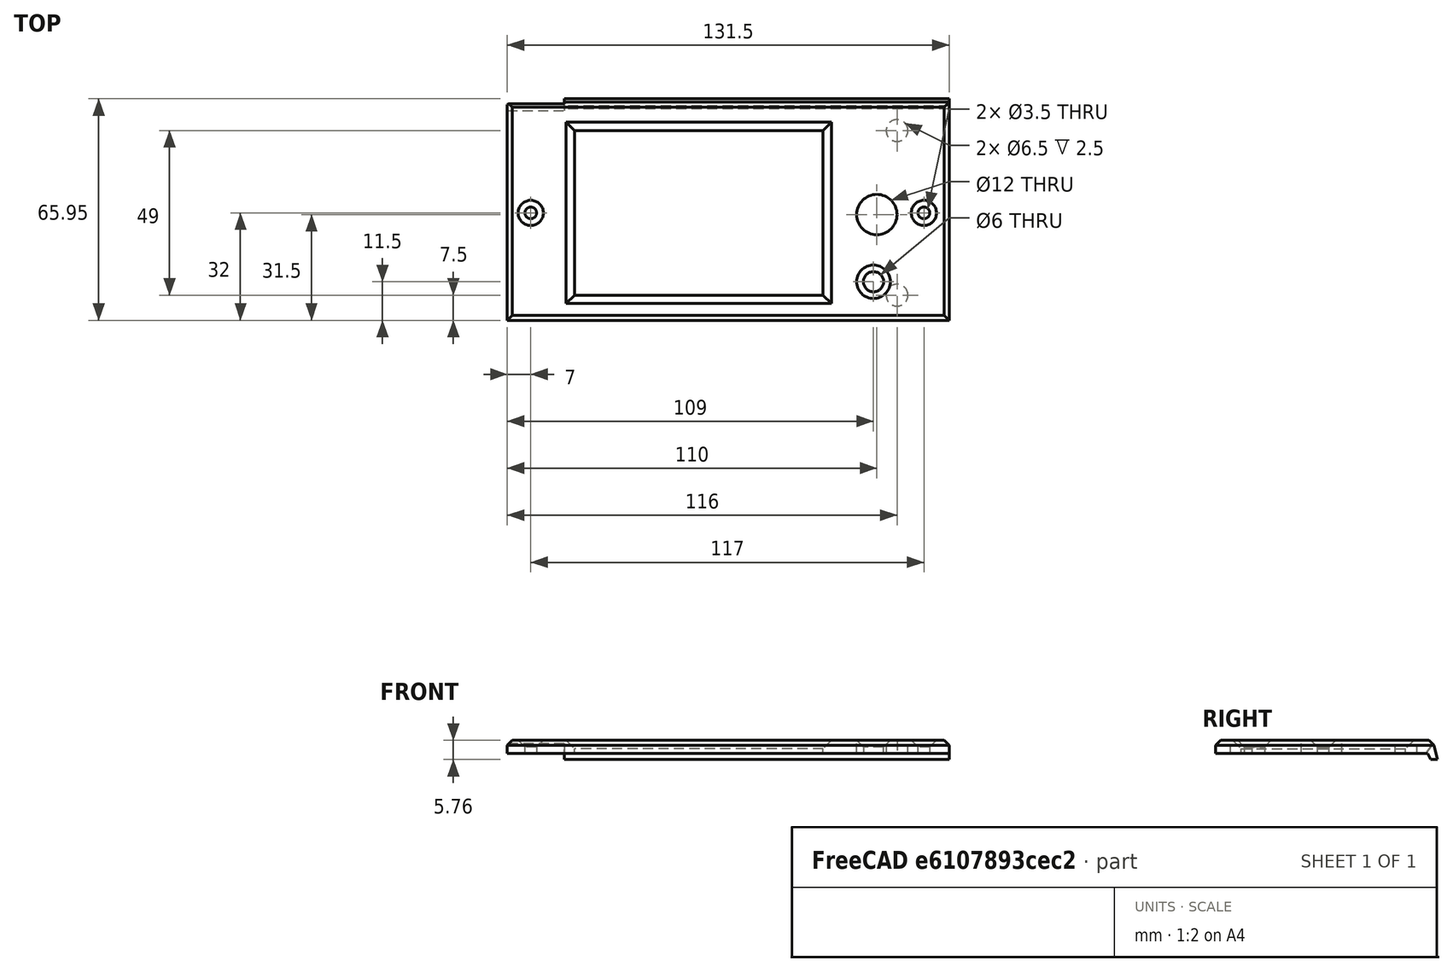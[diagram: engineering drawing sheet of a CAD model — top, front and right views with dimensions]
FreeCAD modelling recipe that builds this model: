
FCSTD DOCUMENT  (FreeCAD 0.19R)
Label: ScreenBezel
License: All rights reserved
LicenseURL: http://en.wikipedia.org/wiki/All_rights_reserved
objects: Sketcher::SketchObject×7, PartDesign::Pocket×5, PartDesign::Chamfer×4, PartDesign::Pad×2, PartDesign::Body×1, Mesh::Feature×1
note: 30 computed .brp shape members not serialized (recipe doc carries the construction recipe); baked Part::Feature solids carry a one-line shape summary decoded from their .brp

FEATURE [Sketcher::SketchObject] Sketch
  FullyConstrained = true
  MapMode = 5
  Support = -> [XY_Plane]
  sketch-geometry (8):
    g0: LineSegment StartX=-59 StartY=33 StartZ=0 EndX=72.5 EndY=33 EndZ=0
    g1: LineSegment StartX=72.5 StartY=33 StartZ=0 EndX=72.5 EndY=-32 EndZ=0
    g2: LineSegment StartX=72.5 StartY=-32 StartZ=0 EndX=-59 EndY=-32 EndZ=0
    g3: LineSegment StartX=-59 StartY=-32 StartZ=0 EndX=-59 EndY=33 EndZ=0
    g4: LineSegment StartX=-39 StartY=24.5 StartZ=0 EndX=35 EndY=24.5 EndZ=0
    g5: LineSegment StartX=35 StartY=24.5 StartZ=0 EndX=35 EndY=-24.5 EndZ=0
    g6: LineSegment StartX=35 StartY=-24.5 StartZ=0 EndX=-39 EndY=-24.5 EndZ=0
    g7: LineSegment StartX=-39 StartY=-24.5 StartZ=0 EndX=-39 EndY=24.5 EndZ=0
  constraints (24):
    c: Coincident(g0,g1)
    c: Coincident(g1,g2)
    c: Coincident(g2,g3)
    c: Coincident(g3,g0)
    c: Horizontal(g0)
    c: Horizontal(g2)
    c: Vertical(g1)
    c: Vertical(g3)
    c: Coincident(g4,g5)
    c: Coincident(g5,g6)
    c: Coincident(g6,g7)
    c: Coincident(g7,g4)
    c: Horizontal(g4)
    c: Horizontal(g6)
    c: Vertical(g5)
    c: Vertical(g7)
    c: Distance(g5) = 49
    c: Distance(g4,g3) = 20
    c: Distance(g0,g5) = 37.5
    c: Distance(g6,g2) = 7.5
    c: Distance(g4,g0) = 8.5
    c: DistanceX(g6) = -39
    c: DistanceY(g6) = -24.5
    c: DistanceX(g4) = 35
FEATURE [PartDesign::Pad] Pad
  Direction = (1,1,1)
  Length = 4
  Length2 = 100
  Profile = -> Sketch
  Type = 0
FEATURE [Sketcher::SketchObject] Sketch001
  ExternalGeometry = -> [Pad]
  FullyConstrained = true
  MapMode = 5
  Placement = pos=(0,0,4) rot=(0,0,1;0rad)
  Support = -> [Pad]
  sketch-geometry (1):
    g0: Circle CenterX=51 CenterY=-0.5 CenterZ=0 NormalX=0 NormalY=0 NormalZ=1 AngleXU=0 Radius=6
  constraints (3):
    c: Distance(g0,g-3) = 16
    c: Diameter(g0) = 12
    c: DistanceY(g0) = -0.5
FEATURE [PartDesign::Pocket] Pocket
  BaseFeature = -> Pad
  Length = 5
  Length2 = 100
  Profile = -> Sketch001
  Type = 0
FEATURE [Sketcher::SketchObject] Sketch002
  ExternalGeometry = -> [Pocket]
  FullyConstrained = true
  MapMode = 5
  Placement = pos=(0,0,0) rot=(1,0,0;3.14159rad)
  Support = -> [Pocket]
  sketch-geometry (2):
    g0: Circle CenterX=57 CenterY=24.5 CenterZ=0 NormalX=0 NormalY=0 NormalZ=1 AngleXU=0 Radius=3.25
    g1: Circle CenterX=57 CenterY=-24.5 CenterZ=0 NormalX=0 NormalY=0 NormalZ=1 AngleXU=0 Radius=3.25
  constraints (5):
    c: Diameter(g1) = 6.5
    c: Equal(g1,g0)
    c: Symmetric(g1,g0,g-1)
    c: Distance(g1,g0) = 49
    c: Distance(g0,g-3) = 22
FEATURE [PartDesign::Pocket] Pocket001
  BaseFeature = -> Pocket
  Length = 2.5
  Length2 = 100
  Profile = -> Sketch002
  Type = 0
FEATURE [Sketcher::SketchObject] Sketch003
  FullyConstrained = true
  MapMode = 5
  Placement = pos=(0,0,4) rot=(0,0,1;0rad)
  Support = -> [Pocket001]
  sketch-geometry (2):
    g0: Circle CenterX=-52 CenterY=0 CenterZ=0 NormalX=0 NormalY=0 NormalZ=1 AngleXU=0 Radius=1.75
    g1: Circle CenterX=65 CenterY=0 CenterZ=0 NormalX=0 NormalY=0 NormalZ=1 AngleXU=0 Radius=1.75
  constraints (6):
    c: Diameter(g1) = 3.5
    c: Equal(g1,g0)
    c: PointOnObject(g0,g-1)
    c: PointOnObject(g1,g-1)
    c: DistanceX(g1) = 65
    c: DistanceX(g0) = -52
FEATURE [PartDesign::Pocket] Pocket002
  BaseFeature = -> Pocket001
  Length = 5
  Length2 = 100
  Profile = -> Sketch003
  Type = 0
FEATURE [Sketcher::SketchObject] Sketch004
  ExternalGeometry = -> [Sketch]
  FullyConstrained = true
  MapMode = 5
  Placement = pos=(0,0,0) rot=(1,0,0;3.14159rad)
  Support = -> [Pocket002]
  sketch-geometry (1):
    g0: Circle CenterX=50 CenterY=20.5 CenterZ=0 NormalX=0 NormalY=0 NormalZ=1 AngleXU=0 Radius=3
  constraints (3):
    c: Distance(g0,g-3) = 15
    c: DistanceY(g0,g-3) = 4
    c: Diameter(g0) = 6
FEATURE [PartDesign::Pocket] Pocket003
  BaseFeature = -> Pocket002
  Length = 5
  Length2 = 100
  Profile = -> Sketch004
  Type = 0
FEATURE [Sketcher::SketchObject] Sketch005
  FullyConstrained = false
  MapMode = 5
  Placement = pos=(72.5,0,0) rot=(0.57735,0.57735,0.57735;2.0944rad)
  Support = -> [Pocket003]
  sketch-geometry (4):
    g0: LineSegment StartX=33 StartY=2.40127 StartZ=0 EndX=33.9475 EndY=-1.76474 EndZ=0
    g1: LineSegment StartX=33.9475 StartY=-1.76474 StartZ=0 EndX=31.8965 EndY=-1.76474 EndZ=0
    g2: LineSegment StartX=31.8965 StartY=-1.76474 StartZ=0 EndX=31 EndY=0 EndZ=0
    g3: LineSegment StartX=31 StartY=0 StartZ=0 EndX=33 EndY=2.40127 EndZ=0
  constraints (8):
    c: Coincident(g0,g1)
    c: Coincident(g1,g2)
    c: DistanceX(g2) = 31
    c: DistanceX(g0) = 33
    c: Horizontal(g1)
    c: PointOnObject(g2,g-1)
    c: Coincident(g2,g3)
    c: Coincident(g3,g0)
FEATURE [PartDesign::Pad] Pad001
  BaseFeature = -> Pocket003
  Direction = (1,1,1)
  Length = 131.5
  Length2 = 100
  Profile = -> Sketch005
  Reversed = true
  Type = 0
FEATURE [PartDesign::Chamfer] Chamfer
  Angle = 45
  Base = -> Pad001 [Edge32]
  BaseFeature = -> Pad001
  ChamferType = 0
  FlipDirection = false
  Size = 1.5
  Size2 = 1
  SupportTransform = false
FEATURE [PartDesign::Chamfer] Chamfer001
  Angle = 45
  Base = -> Chamfer [Edge1,Edge7,Edge9]
  BaseFeature = -> Chamfer
  ChamferType = 0
  FlipDirection = false
  Size = 1.5
  Size2 = 1
  SupportTransform = false
FEATURE [Sketcher::SketchObject] Sketch006
  FullyConstrained = false
  MapMode = 5
  Placement = pos=(-59,0,0) rot=(-0.57735,0.57735,0.57735;4.18879rad)
  sketch-geometry (4):
    g0: LineSegment StartX=-34.2358 StartY=5.38851 StartZ=0 EndX=-28.5 EndY=-2.80301 EndZ=0
    g1: LineSegment StartX=-28.5 StartY=-2.80301 StartZ=0 EndX=-36.6915 EndY=-8.53878 EndZ=0
    g2: LineSegment StartX=-36.6915 StartY=-8.53878 StartZ=0 EndX=-42.4273 EndY=-0.347258 EndZ=0
    g3: LineSegment StartX=-42.4273 StartY=-0.347258 StartZ=0 EndX=-34.2358 EndY=5.38851 EndZ=0
  constraints (11):
    c: Coincident(g0,g1)
    c: Coincident(g1,g2)
    c: Coincident(g2,g3)
    c: Coincident(g3,g0)
    c: Angle(g3) = 0.610865
    c: Perpendicular(g3,g0)
    c: Perpendicular(g0,g1)
    c: Distance(g0) = 10
    c: Perpendicular(g2,g1)
    c: Equal(g0,g3)
    c: DistanceX(g0) = -28.5
FEATURE [PartDesign::Chamfer] Chamfer002
  Angle = 45
  Base = -> Chamfer001 [Edge38,Edge40,Edge41,Edge39]
  BaseFeature = -> Chamfer001
  ChamferType = 0
  FlipDirection = false
  Size = 2.5
  Size2 = 1
  SupportTransform = false
FEATURE [PartDesign::Chamfer] Chamfer003
  Angle = 45
  Base = -> Chamfer002 [Edge11,Edge12,Edge9]
  BaseFeature = -> Chamfer002
  ChamferType = 0
  FlipDirection = false
  Size = 2
  Size2 = 1
  SupportTransform = false
FEATURE [PartDesign::Pocket] Pocket004
  BaseFeature = -> Chamfer003
  Length = 17
  Length2 = 100
  Profile = -> Sketch006
  Type = 0
FEATURE [PartDesign::Body] Body
  Group = -> [Sketch,Pad,Sketch001,Pocket,Sketch002,Pocket001,Sketch003,Pocket002,Sketch004,Pocket003,Sketch005,Pad001,Chamfer,Chamfer001,Sketch006,Chamfer002,Chamfer003,Pocket004]
  Origin = -> Origin
  Tip = -> Pocket004
FEATURE [Mesh::Feature] Mesh  label="Pocket004 (Meshed)"
